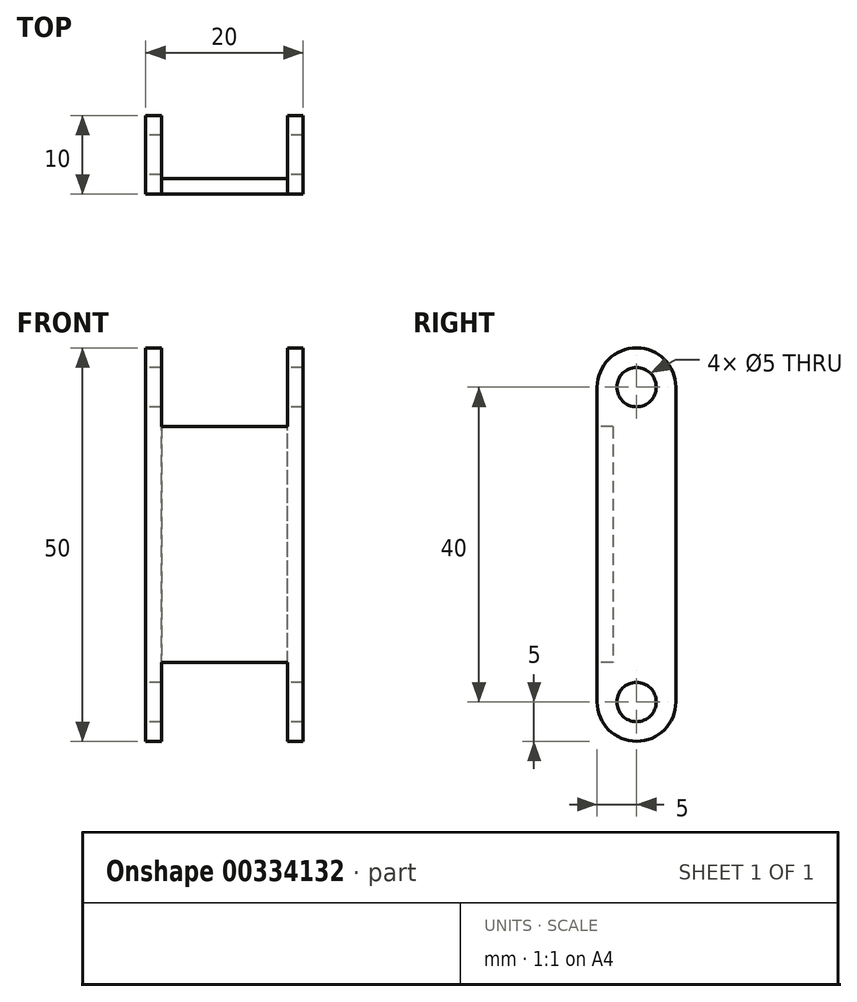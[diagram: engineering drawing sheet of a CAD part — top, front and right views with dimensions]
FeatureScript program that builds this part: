
annotation { "Feature Type Name" : "Feature", "Feature Type Description" : "" }
export const myFeature = defineFeature(function(context is Context, id is Id, definition is map)
    precondition{}
    {
        {
            var Q0;
            Q0=qCreatedBy(makeId("Front.planeOp"),FACE);
            var sketch = newSketch(context, id + "F0", { "sketchPlane" : qUnion([Q0])});
            skLineSegment(sketch, "E0.bottom", {"start": v(0, 0) * mm, "end": v(2, 0) * mm});
            skLineSegment(sketch, "E0.top", {"start": v(0, 50) * mm, "end": v(2, 50) * mm});
            skLineSegment(sketch, "E0.left", {"start": v(0, 0) * mm, "end": v(0, 50) * mm});
            skLineSegment(sketch, "E0.right", {"start": v(2, 0) * mm, "end": v(2, 50) * mm});
            skLineSegment(sketch, "E1.bottom", {"start": v(2, 40) * mm, "end": v(18, 40) * mm});
            skLineSegment(sketch, "E1.top", {"start": v(2, 10) * mm, "end": v(18, 10) * mm});
            skLineSegment(sketch, "E1.left", {"start": v(2, 40) * mm, "end": v(2, 10) * mm});
            skLineSegment(sketch, "E1.right", {"start": v(18, 40) * mm, "end": v(18, 10) * mm});
            skPoint(sketch, "E1.middle", {"position": v(10, 25) * mm});
            skPoint(sketch, "E1.middle.positionSnap0", {"position": v(2, 25) * mm});
            skPoint(sketch, "E1.centerSnap0", {"position": v(2, 25) * mm});
            skLineSegment(sketch, "E2", {"start": v(10, 42.57) * mm, "end": v(10, 7.33) * mm, "construction": true});
            skLineSegment(sketch, "E3.MirrorCS", {"start": v(18, 0) * mm, "end": v(18, 50) * mm});
            skLineSegment(sketch, "E4.MirrorCS", {"start": v(20, 50) * mm, "end": v(18, 50) * mm});
            skLineSegment(sketch, "E5.MirrorCS", {"start": v(20, 0) * mm, "end": v(20, 50) * mm});
            skLineSegment(sketch, "E6.MirrorCS", {"start": v(20, 0) * mm, "end": v(18, 0) * mm});
            skSolve(sketch);
        }
        {
            var Q0;
            {var subQ1=sQuery(id+"F0.wireOp",EDGE,"E0.bottom");Q0=makeQuery(id+"F0.imprint","IMPRINT",FACE,{"disambiguationData":[TD([[makeQuery(id+"F0.imprint","IMPRINT",EDGE,{"derivedFrom":subQ1}),1.0]])]});}
            var Q1;
            {var subQ0=sQuery(id+"F0.wireOp",EDGE,"E4.MirrorCS");Q1=makeQuery(id+"F0.imprint","IMPRINT",FACE,{"disambiguationData":[TD([[makeQuery(id+"F0.imprint","IMPRINT",EDGE,{"derivedFrom":subQ0}),1.0]])]});}
            extrude(context, id + "F1", {"entities" : qUnion([Q0, Q1]), "depth" : 10 * mm, "symmetric" : true});
        }
        {
            var Q0;
            Q0=makeQuery(id+"F1.opExtrude","SWEPT_FACE",FACE,{"disambiguationData":[OSD([sQuery(id+"F0.wireOp",EDGE,"E0.left")])]});
            var sketch = newSketch(context, id + "F2", { "sketchPlane" : qUnion([Q0])});
            skArc(sketch, "E7", {"start": v(-5, 5) * mm, "mid": v(0, 0) * mm, "end": v(5, 5) * mm});
            skLineSegment(sketch, "E8.0", {"start": v(5, 0) * mm, "end": v(5, 5) * mm});
            skLineSegment(sketch, "E9.0", {"start": v(-5, 0) * mm, "end": v(-5, 5) * mm});
            skLineSegment(sketch, "E10.0", {"start": v(5, 0) * mm, "end": v(-5, 0) * mm});
            skPoint(sketch, "E11.orphan", {"position": v(5, 50) * mm});
            skPoint(sketch, "E12.orphan", {"position": v(-5, 50) * mm});
            skSolve(sketch);
        }
        {
            var Q0;
            Q0=qSketchRegion(id+"F2",true);
            extrude(context, id + "F3", {"entities" : qUnion([Q0]), "operationType" : NewBodyOperationType.REMOVE, "oppositeDirection" : true, "depth" : 25 * mm});
        }
        {
            var Q0;
            Q0=makeQuery(id+"F1.opExtrude","SWEPT_FACE",FACE,{"disambiguationData":[OSD([sQuery(id+"F0.wireOp",EDGE,"E0.left")])]});
            var sketch = newSketch(context, id + "F4", { "sketchPlane" : qUnion([Q0])});
            skArc(sketch, "E13", {"start": v(5, 45) * mm, "mid": v(0, 50) * mm, "end": v(-5, 45) * mm});
            skLineSegment(sketch, "E14.0", {"start": v(5, 50) * mm, "end": v(-5, 50) * mm});
            skLineSegment(sketch, "E15.0", {"start": v(-5, 45) * mm, "end": v(-5, 50) * mm});
            skLineSegment(sketch, "E16.0", {"start": v(5, 45) * mm, "end": v(5, 50) * mm});
            skPoint(sketch, "E17.orphan", {"position": v(5, 5) * mm});
            skPoint(sketch, "E18.orphan", {"position": v(-5, 5) * mm});
            skSolve(sketch);
        }
        {
            var Q0;
            Q0=qSketchRegion(id+"F4",true);
            extrude(context, id + "F5", {"entities" : qUnion([Q0]), "operationType" : NewBodyOperationType.REMOVE, "oppositeDirection" : true, "depth" : 25 * mm});
        }
        {
            var Q0;
            Q0=makeQuery(id+"F1.opExtrude","SWEPT_FACE",FACE,{"disambiguationData":[OSD([sQuery(id+"F0.wireOp",EDGE,"E0.left")])]});
            var sketch = newSketch(context, id + "F6", { "sketchPlane" : qUnion([Q0])});
            skCircle(sketch, "E19", {"center": v(0, 45) * mm, "radius": 2.5 * mm});
            skSolve(sketch);
        }
        {
            var Q0;
            Q0=qSketchRegion(id+"F6",true);
            extrude(context, id + "F7", {"entities" : qUnion([Q0]), "operationType" : NewBodyOperationType.REMOVE, "oppositeDirection" : true, "depth" : 25 * mm});
        }
        {
            var Q0;
            Q0=makeQuery(id+"F1.opExtrude","SWEPT_FACE",FACE,{"disambiguationData":[OSD([sQuery(id+"F0.wireOp",EDGE,"E0.left")])]});
            var sketch = newSketch(context, id + "F8", { "sketchPlane" : qUnion([Q0])});
            skCircle(sketch, "E20", {"center": v(0, 5) * mm, "radius": 2.5 * mm});
            skSolve(sketch);
        }
        {
            var Q0;
            Q0=qSketchRegion(id+"F8",true);
            extrude(context, id + "F9", {"entities" : qUnion([Q0]), "operationType" : NewBodyOperationType.REMOVE, "oppositeDirection" : true, "depth" : 25 * mm});
        }
        {
            var Q0;
            Q0=makeQuery(id+"F1.opExtrude","CAP_FACE",FACE,{"disambiguationData":[OSD([sQuery(id+"F0.wireOp",EDGE,"E3.MirrorCS"),sQuery(id+"F0.wireOp",EDGE,"E4.MirrorCS"),sQuery(id+"F0.wireOp",EDGE,"E5.MirrorCS"),sQuery(id+"F0.wireOp",EDGE,"E6.MirrorCS")])],"isStart":false});
            var sketch = newSketch(context, id + "F10", { "sketchPlane" : qUnion([Q0])});
            skLineSegment(sketch, "E21.0", {"start": v(2, 40) * mm, "end": v(18, 40) * mm});
            skLineSegment(sketch, "E22.0", {"start": v(2, 10) * mm, "end": v(18, 10) * mm});
            skLineSegment(sketch, "E23.0", {"start": v(2, 40) * mm, "end": v(2, 10) * mm});
            skLineSegment(sketch, "E24.0", {"start": v(18, 10) * mm, "end": v(18, 40) * mm});
            skPoint(sketch, "E25.orphan", {"position": v(18, 50) * mm});
            skPoint(sketch, "E26.orphan", {"position": v(18, 0) * mm});
            skSolve(sketch);
        }
        {
            var Q0;
            Q0=qSketchRegion(id+"F10",true);
            extrude(context, id + "F11", {"entities" : qUnion([Q0]), "oppositeDirection" : true, "depth" : 2 * mm});
        }
        {
            var Q0;
            Q0=makeQuery(id+"F1.opExtrude","SWEPT_BODY",BODY,{"disambiguationData":[OSD([sQuery(id+"F0.wireOp",EDGE,"E0.bottom"),sQuery(id+"F0.wireOp",EDGE,"E0.top"),sQuery(id+"F0.wireOp",EDGE,"E0.left"),sQuery(id+"F0.wireOp",EDGE,"E0.right"),sQuery(id+"F0.wireOp",EDGE,"E1.left")])]});
            var Q1;
            Q1=makeQuery(id+"F1.opExtrude","SWEPT_BODY",BODY,{"disambiguationData":[OSD([sQuery(id+"F0.wireOp",EDGE,"E3.MirrorCS"),sQuery(id+"F0.wireOp",EDGE,"E4.MirrorCS"),sQuery(id+"F0.wireOp",EDGE,"E5.MirrorCS"),sQuery(id+"F0.wireOp",EDGE,"E6.MirrorCS")])]});
            var Q2;
            Q2=makeQuery(id+"F11.opExtrude","SWEPT_BODY",BODY,{"disambiguationData":[OSD([sQuery(id+"F10.wireOp",EDGE,"E21.0"),sQuery(id+"F10.wireOp",EDGE,"E22.0"),sQuery(id+"F10.wireOp",EDGE,"E23.0"),sQuery(id+"F10.wireOp",EDGE,"E24.0")])]});
            booleanBodies(context, id + "F12", {"operationType" : BooleanOperationType.UNION, "tools" : qUnion([Q0, Q1, Q2])});
        }
        {
            var Q0;
            Q0=makeQuery(id+"F1.opExtrude","SWEPT_FACE",FACE,{"disambiguationData":[OSD([sQuery(id+"F0.wireOp",EDGE,"E5.MirrorCS")])]});
            var sketch = newSketch(context, id + "F13", { "sketchPlane" : qUnion([Q0])});
            skArc(sketch, "E27", {"start": v(5, 45) * mm, "mid": v(0, 50) * mm, "end": v(-5, 45) * mm});
            skCircle(sketch, "E28", {"center": v(0, 45) * mm, "radius": 2.5 * mm});
            skArc(sketch, "E29", {"start": v(-5, 5) * mm, "mid": v(0, 0) * mm, "end": v(5, 5) * mm});
            skCircle(sketch, "E30", {"center": v(0, 5) * mm, "radius": 2.5 * mm});
            skLineSegment(sketch, "E31.0", {"start": v(-5, 50) * mm, "end": v(5, 50) * mm});
            skLineSegment(sketch, "E32.0", {"start": v(5, 0) * mm, "end": v(5, 5) * mm});
            skLineSegment(sketch, "E33.0", {"start": v(-5, 0) * mm, "end": v(-5, 5) * mm});
            skLineSegment(sketch, "E34.0", {"start": v(-5, 0) * mm, "end": v(5, 0) * mm});
            skLineSegment(sketch, "E35.trimOffspring", {"start": v(-5, 45) * mm, "end": v(-5, 50) * mm});
            skLineSegment(sketch, "E36.trimOffspring", {"start": v(5, 45) * mm, "end": v(5, 50) * mm});
            skSolve(sketch);
        }
        {
            var Q0;
            Q0=qSketchRegion(id+"F13",true);
            extrude(context, id + "F14", {"entities" : qUnion([Q0]), "operationType" : NewBodyOperationType.REMOVE, "oppositeDirection" : true, "depth" : 10 * mm});
        }
    });
